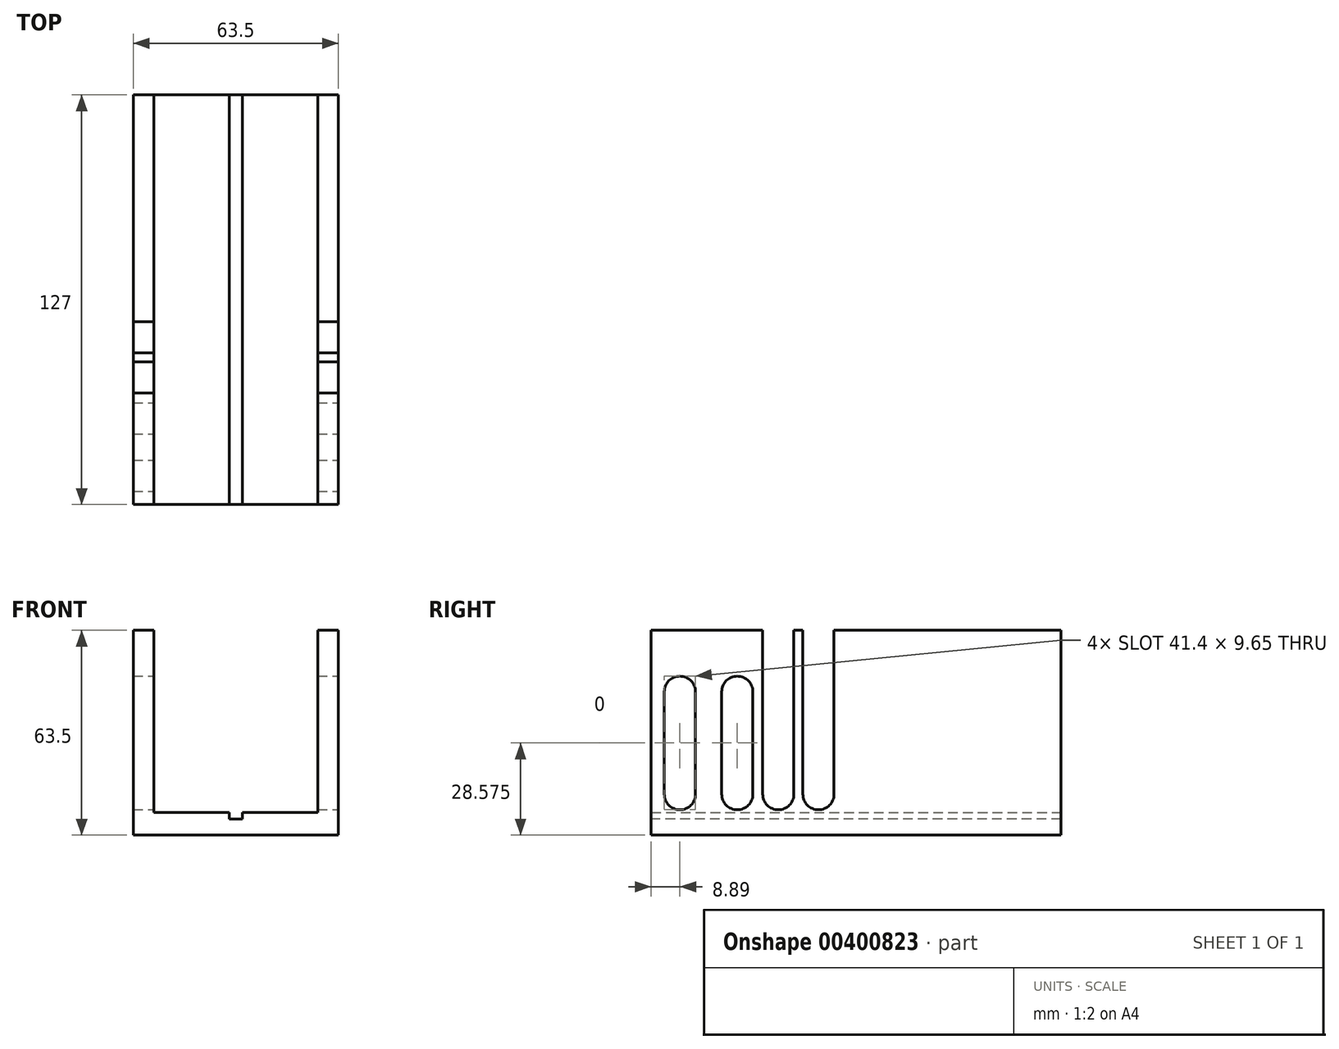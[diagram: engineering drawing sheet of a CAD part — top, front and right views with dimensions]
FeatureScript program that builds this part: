
annotation { "Feature Type Name" : "Feature", "Feature Type Description" : "" }
export const myFeature = defineFeature(function(context is Context, id is Id, definition is map)
    precondition{}
    {
        {
            var Q0;
            Q0=qCreatedBy(makeId("Front.planeOp"),FACE);
            var sketch = newSketch(context, id + "F0", { "sketchPlane" : qUnion([Q0])});
            skLineSegment(sketch, "E0.bottom", {"start": v(31.75, 31.75) * mm, "end": v(25.4, 31.75) * mm});
            skLineSegment(sketch, "E0.top", {"start": v(31.75, -31.75) * mm, "end": v(-31.75, -31.75) * mm});
            skLineSegment(sketch, "E0.left", {"start": v(31.75, 31.75) * mm, "end": v(31.75, -31.75) * mm});
            skLineSegment(sketch, "E0.right", {"start": v(-31.75, 31.75) * mm, "end": v(-31.75, -31.75) * mm});
            skPoint(sketch, "E0.middle", {"position": v(0, 0) * mm});
            skLineSegment(sketch, "E1.top", {"start": v(25.4, -24.71) * mm, "end": v(-25.4, -24.71) * mm});
            skLineSegment(sketch, "E1.left", {"start": v(25.4, 31.75) * mm, "end": v(25.4, -24.71) * mm});
            skLineSegment(sketch, "E1.right", {"start": v(-25.4, 31.75) * mm, "end": v(-25.4, -24.71) * mm});
            skLineSegment(sketch, "E2.trimOffspring", {"start": v(-25.4, 31.75) * mm, "end": v(-31.75, 31.75) * mm});
            skSolve(sketch);
        }
        {
            var Q0;
            Q0 = qSketchRegion(id + "F0", true);
            extrude(context, id + "F1", {"entities" : qUnion([Q0]), "endBound" : BoundingType.SYMMETRIC, "depth" : 127 * mm});
        }
        {
            var Q0;
            Q0=makeQuery(id+"F1.opExtrude","SWEPT_FACE",FACE,{"disambiguationData":[OSD([sQuery(id+"F0.wireOp",EDGE,"E0.left")])]});
            var sketch = newSketch(context, id + "F2", { "sketchPlane" : qUnion([Q0])});
            skCircle(sketch, "E3", {"center": v(-54.6, 12.7) * mm, "radius": 4.83 * mm});
            skCircle(sketch, "E4", {"center": v(-54.6, -19.05) * mm, "radius": 4.83 * mm});
            skCircle(sketch, "E5", {"center": v(-36.83, 12.7) * mm, "radius": 4.83 * mm});
            skCircle(sketch, "E6", {"center": v(-36.83, -19.05) * mm, "radius": 4.83 * mm});
            skLineSegment(sketch, "E7", {"start": v(-59.44, 12.7) * mm, "end": v(-59.44, -19.05) * mm});
            skLineSegment(sketch, "E8", {"start": v(-49.78, 12.7) * mm, "end": v(-49.78, -19.05) * mm});
            skLineSegment(sketch, "E9", {"start": v(-41.66, 12.7) * mm, "end": v(-41.66, -19.05) * mm});
            skLineSegment(sketch, "E10", {"start": v(-32, 12.7) * mm, "end": v(-32, -19.05) * mm});
            skSolve(sketch);
        }
        {
            var Q0;
            Q0 = qSketchRegion(id + "F2", true);
            extrude(context, id + "F3", {"entities" : qUnion([Q0]), "operationType" : NewBodyOperationType.REMOVE, "endBound" : BoundingType.THROUGH_ALL, "oppositeDirection" : true, "depth" : 25.4 * mm});
        }
        {
            var Q0;
            Q0=qCreatedBy(makeId("Front.planeOp"),FACE);
            var sketch = newSketch(context, id + "F4", { "sketchPlane" : qUnion([Q0])});
            skLineSegment(sketch, "E11.bottom", {"start": v(-2, -24.71) * mm, "end": v(2, -24.71) * mm});
            skLineSegment(sketch, "E11.top", {"start": v(-2, -26.75) * mm, "end": v(2, -26.75) * mm});
            skLineSegment(sketch, "E11.left", {"start": v(-2, -24.71) * mm, "end": v(-2, -26.75) * mm});
            skLineSegment(sketch, "E11.right", {"start": v(2, -24.71) * mm, "end": v(2, -26.75) * mm});
            skSolve(sketch);
        }
        {
            var Q0;
            Q0 = qSketchRegion(id + "F4", true);
            extrude(context, id + "F5", {"entities" : qUnion([Q0]), "operationType" : NewBodyOperationType.REMOVE, "endBound" : BoundingType.SYMMETRIC, "oppositeDirection" : true, "depth" : 127 * mm});
        }
        {
            var Q0;
            Q0=makeQuery(id+"F1.opExtrude","SWEPT_FACE",FACE,{"disambiguationData":[OSD([sQuery(id+"F0.wireOp",EDGE,"E0.left")])]});
            var sketch = newSketch(context, id + "F6", { "sketchPlane" : qUnion([Q0])});
            skCircle(sketch, "E12", {"center": v(-24.13, -19.05) * mm, "radius": 4.83 * mm});
            skCircle(sketch, "E13", {"center": v(-11.68, -19.05) * mm, "radius": 4.83 * mm});
            skLineSegment(sketch, "E14", {"start": v(-28.96, -19.05) * mm, "end": v(-28.96, 31.75) * mm});
            skLineSegment(sketch, "E15", {"start": v(-19.3, -19.05) * mm, "end": v(-19.3, 31.75) * mm});
            skLineSegment(sketch, "E16", {"start": v(-16.5, -19.05) * mm, "end": v(-16.5, 31.75) * mm});
            skLineSegment(sketch, "E17", {"start": v(-6.86, -19.05) * mm, "end": v(-6.86, 31.75) * mm});
            skSolve(sketch);
        }
        {
            var Q0;
            Q0 = qSketchRegion(id + "F6", true);
            var Q1;
            {var subQ0=sQuery(id+"F6.wireOp",EDGE,"E14");Q1=makeQuery(id+"F6.imprint","IMPRINT",FACE,{"disambiguationData":[TD([[makeQuery(id+"F6.imprint","IMPRINT",EDGE,{"derivedFrom":subQ0}),-1.0]])]});}
            var Q2;
            {var subQ0=sQuery(id+"F6.wireOp",EDGE,"E16");Q2=makeQuery(id+"F6.imprint","IMPRINT",FACE,{"disambiguationData":[TD([[makeQuery(id+"F6.imprint","IMPRINT",EDGE,{"derivedFrom":subQ0}),-1.0]])]});}
            extrude(context, id + "F7", {"entities" : qUnion([Q0, Q1, Q2]), "operationType" : NewBodyOperationType.REMOVE, "endBound" : BoundingType.THROUGH_ALL, "oppositeDirection" : true, "depth" : 25.4 * mm});
        }
    });
